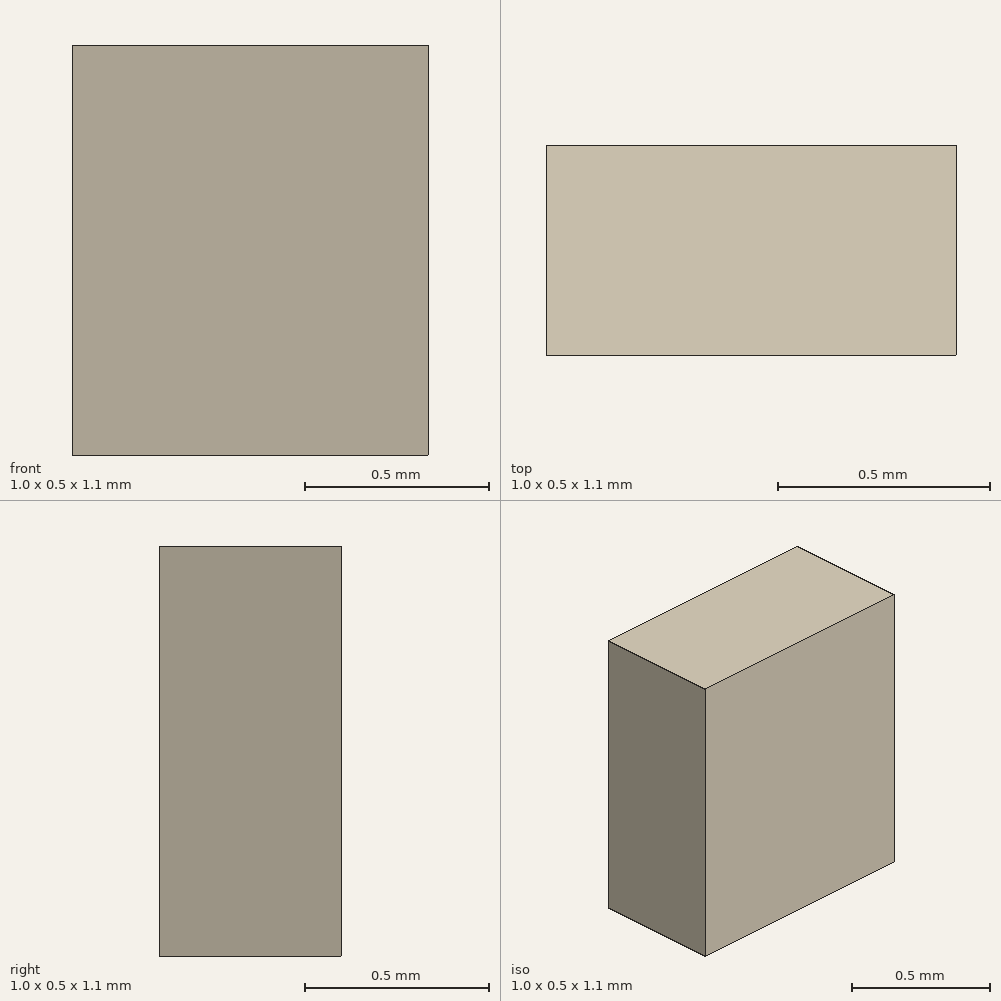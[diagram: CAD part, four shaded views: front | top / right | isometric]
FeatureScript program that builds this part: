
annotation { "Feature Type Name" : "Feature", "Feature Type Description" : "" }
export const myFeature = defineFeature(function(context is Context, id is Id, definition is map)
    precondition{}
    {
        {
            var Q0;
            Q0=qCreatedBy(makeId("Top.planeOp"),FACE);
            var sketch = newSketch(context, id + "F0", { "sketchPlane" : qUnion([Q0])});
            skLineSegment(sketch, "E0.bottom", {"start": v(0, 0) * mm, "end": v(0.97, 0) * mm});
            skLineSegment(sketch, "E0.top", {"start": v(0, 0.5) * mm, "end": v(0.97, 0.5) * mm});
            skLineSegment(sketch, "E0.left", {"start": v(0, 0) * mm, "end": v(0, 0.5) * mm});
            skLineSegment(sketch, "E0.right", {"start": v(0.97, 0) * mm, "end": v(0.97, 0.5) * mm});
            skSolve(sketch);
        }
        {
            var Q0;
            Q0=makeQuery(id+"F0.imprint","IMPRINT",FACE,{"disambiguationData":[TD([[makeQuery(id+"F0.imprint","IMPRINT",EDGE,{"derivedFrom":sQuery(id+"F0.wireOp",EDGE,"E0.bottom")}),1.0]])]});
            extrude(context, id + "F1", {"entities" : qUnion([Q0]), "depth" : 1.12 * mm});
        }
    });
